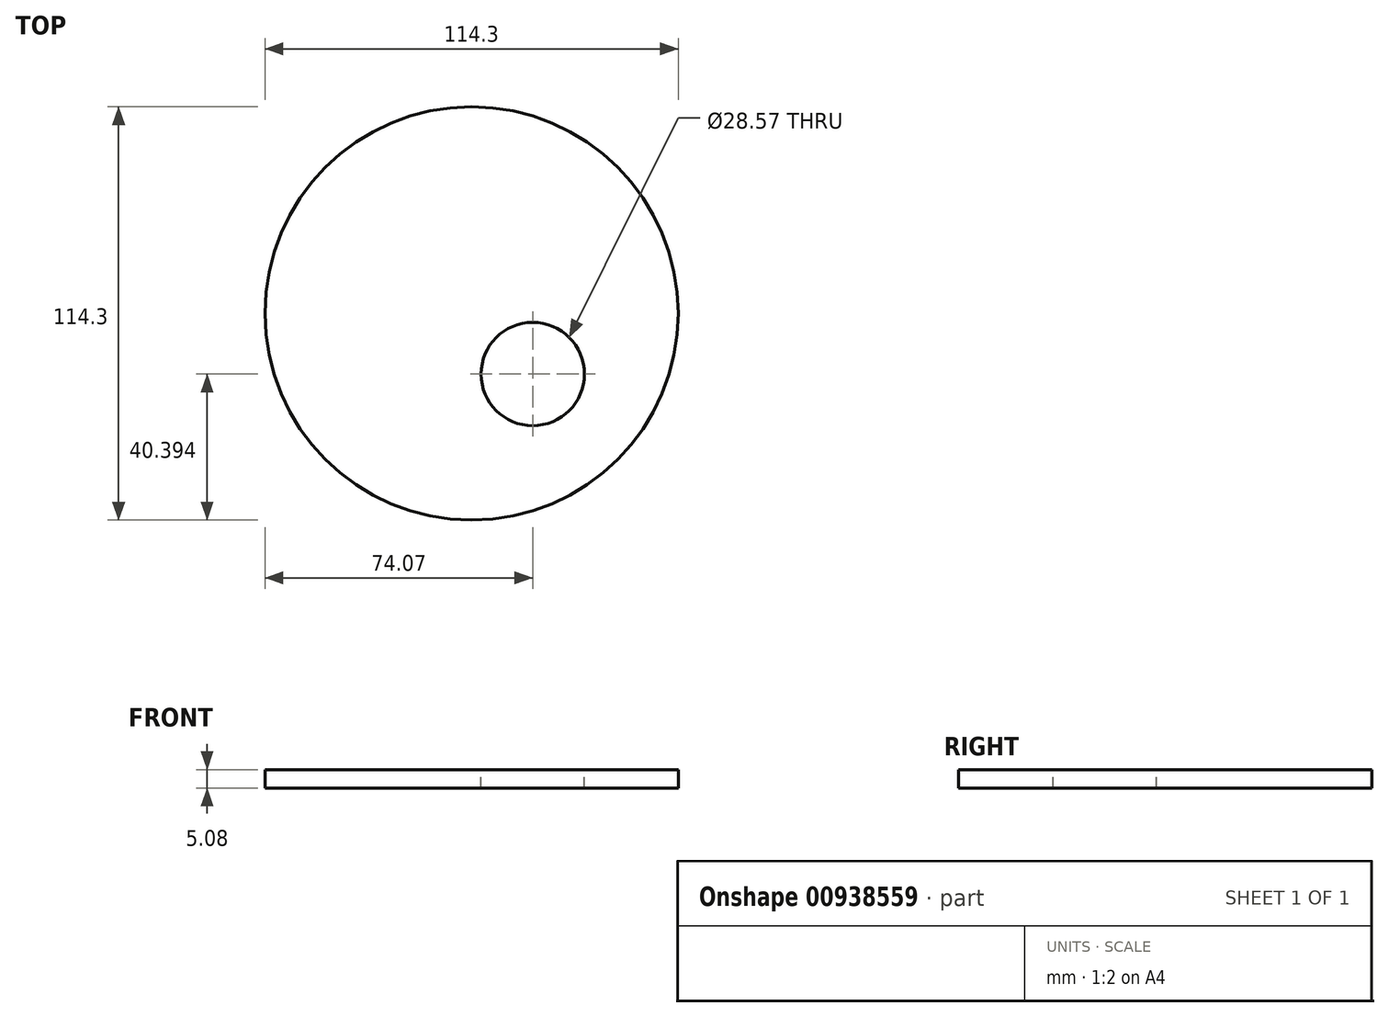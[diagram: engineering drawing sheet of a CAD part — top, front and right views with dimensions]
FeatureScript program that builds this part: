
annotation { "Feature Type Name" : "Feature", "Feature Type Description" : "" }
export const myFeature = defineFeature(function(context is Context, id is Id, definition is map)
    precondition{}
    {
        {
            var Q0;
            Q0=qCreatedBy(makeId("Top.planeOp"),FACE);
            var sketch = newSketch(context, id + "F0", { "sketchPlane" : qUnion([Q0])});
            skCircle(sketch, "E0", {"center": v(0, 0) * mm, "radius": 57.15 * mm});
            skSolve(sketch);
        }
        {
            var Q0;
            Q0 = qSketchRegion(id + "F0", true);
            extrude(context, id + "F1", {"entities" : qUnion([Q0]), "depth" : 5.08 * mm, "offsetDistance" : 25.4 * mm});
        }
        {
            var Q0;
            Q0=makeQuery(id+"F1.opExtrude","CAP_FACE",FACE,{"disambiguationData":[OSD([sQuery(id+"F0.wireOp",EDGE,"E0")])],"isStart":false});
            var sketch = newSketch(context, id + "F2", { "sketchPlane" : qUnion([Q0])});
            skLineSegment(sketch, "E1", {"start": v(0, 0) * mm, "end": v(40.6, -40.21) * mm});
            skLineSegment(sketch, "E2", {"start": v(0, 0) * mm, "end": v(16.92, -16.76) * mm});
            skPoint(sketch, "E3", {"position": v(16.92, -16.76) * mm});
            skCircle(sketch, "E4", {"center": v(16.92, -16.76) * mm, "radius": 14.29 * mm});
            skSolve(sketch);
        }
        {
            var Q0;
            Q0 = qSketchRegion(id + "F2", true);
            extrude(context, id + "F3", {"entities" : qUnion([Q0]), "operationType" : NewBodyOperationType.REMOVE, "oppositeDirection" : true, "depth" : 6.35 * mm, "offsetDistance" : 25.4 * mm});
        }
    });
